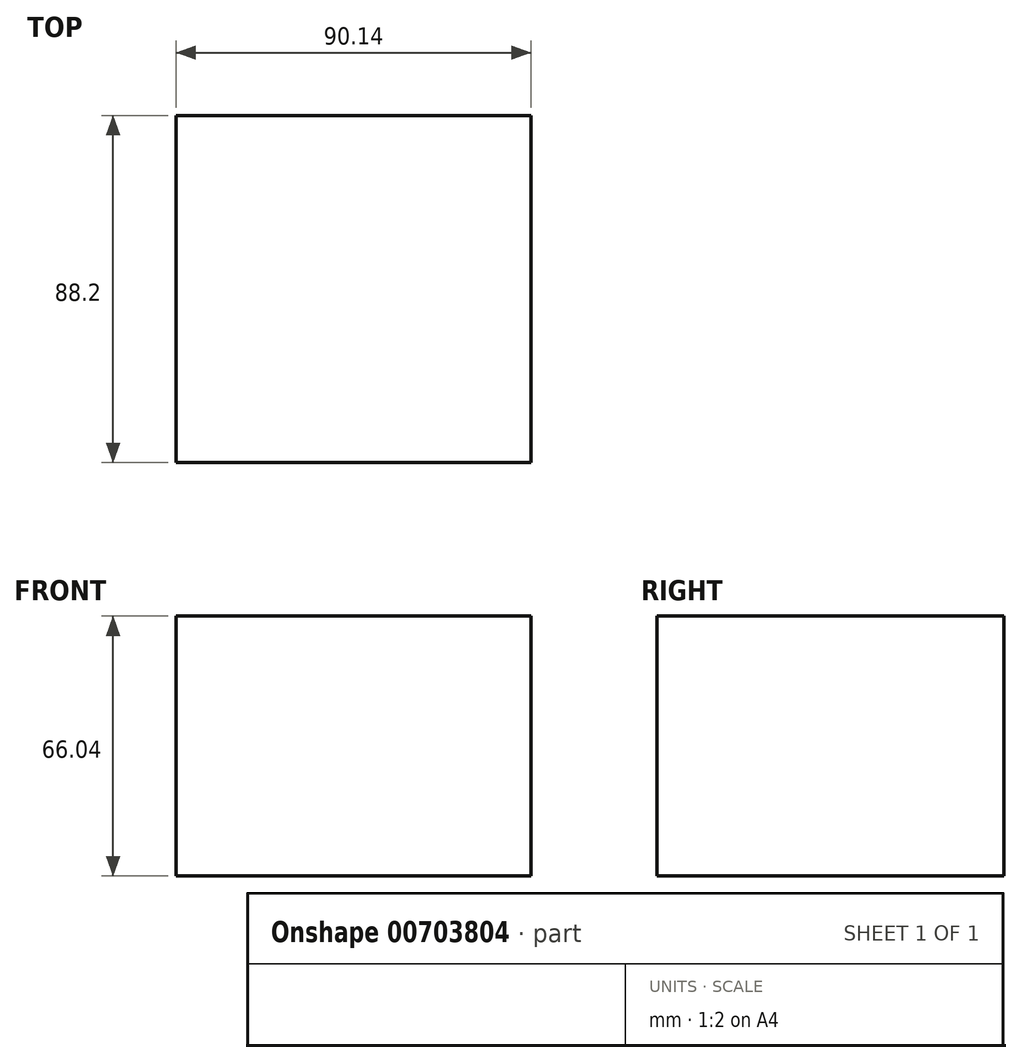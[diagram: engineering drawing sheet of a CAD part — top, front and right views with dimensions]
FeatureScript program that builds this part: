
annotation { "Feature Type Name" : "Feature", "Feature Type Description" : "" }
export const myFeature = defineFeature(function(context is Context, id is Id, definition is map)
    precondition{}
    {
        {
            var Q0;
            Q0=qCreatedBy(makeId("Top.planeOp"),FACE);
            var sketch = newSketch(context, id + "F0", { "sketchPlane" : qUnion([Q0])});
            skLineSegment(sketch, "E0.bottom", {"start": v(45.07, -44.1) * mm, "end": v(-45.07, -44.1) * mm});
            skLineSegment(sketch, "E0.top", {"start": v(45.07, 44.1) * mm, "end": v(-45.07, 44.1) * mm});
            skLineSegment(sketch, "E0.left", {"start": v(45.07, -44.1) * mm, "end": v(45.07, 44.1) * mm});
            skLineSegment(sketch, "E0.right", {"start": v(-45.07, -44.1) * mm, "end": v(-45.07, 44.1) * mm});
            skPoint(sketch, "E0.middle", {"position": v(0, 0) * mm});
            skSolve(sketch);
        }
        {
            var Q0;
            Q0=makeQuery(id+"F0.imprint","IMPRINT",FACE,{"disambiguationData":[TD([[makeQuery(id+"F0.imprint","IMPRINT",EDGE,{"derivedFrom":sQuery(id+"F0.wireOp",EDGE,"E0.bottom")}),-1.0]])]});
            extrude(context, id + "F1", {"entities" : qUnion([Q0]), "depth" : 66.04 * mm, "offsetDistance" : 25.4 * mm});
        }
    });
